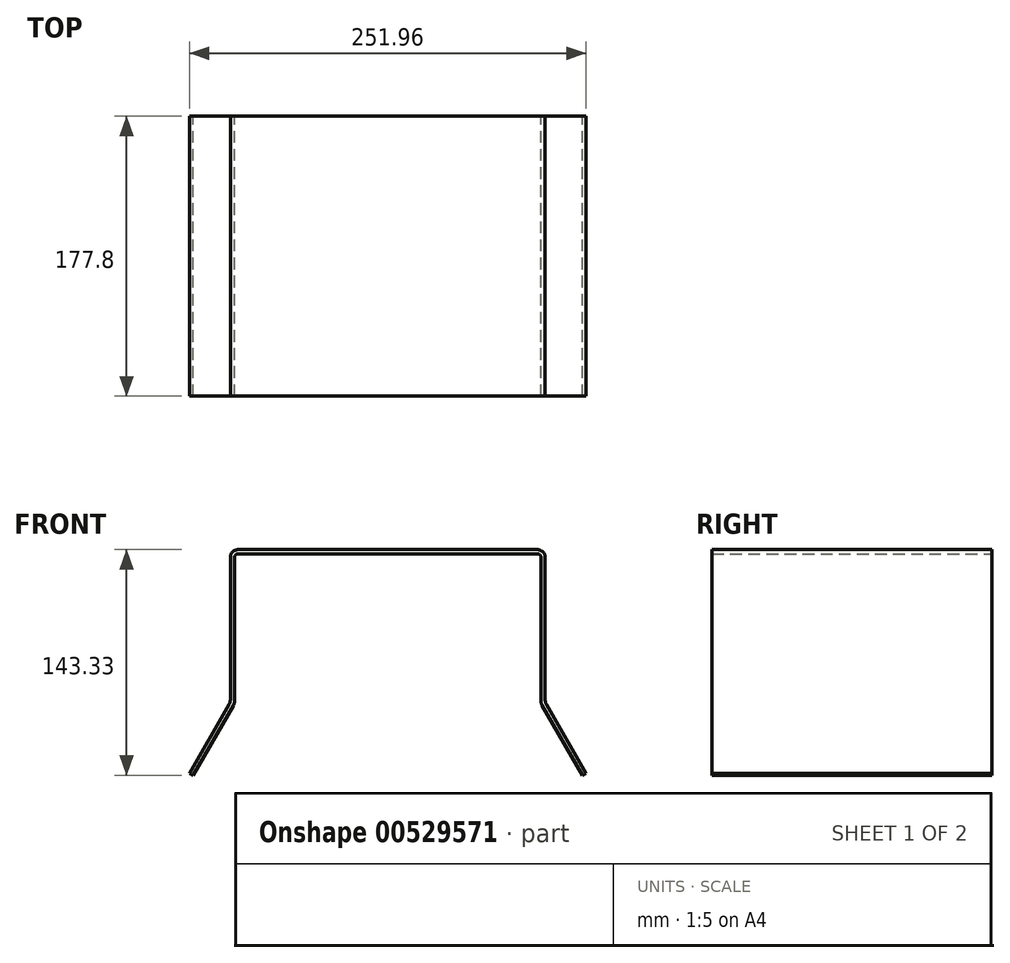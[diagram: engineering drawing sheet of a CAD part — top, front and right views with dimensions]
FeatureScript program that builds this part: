
annotation { "Feature Type Name" : "Feature", "Feature Type Description" : "" }
export const myFeature = defineFeature(function(context is Context, id is Id, definition is map)
    precondition{}
    {
        {
            var Q0;
            Q0=qCreatedBy(makeId("Front.planeOp"),FACE);
            var sketch = newSketch(context, id + "F0", { "sketchPlane" : qUnion([Q0])});
            skLineSegment(sketch, "E0", {"start": v(5, 0) * mm, "end": v(195, 0) * mm});
            skLineSegment(sketch, "E1", {"start": v(200, -5) * mm, "end": v(200, -97) * mm});
            skLineSegment(sketch, "E2", {"start": v(200, -97) * mm, "end": v(225.98, -142) * mm});
            skLineSegment(sketch, "E3", {"start": v(0, -5) * mm, "end": v(0, -97) * mm});
            skLineSegment(sketch, "E4", {"start": v(0, -97) * mm, "end": v(-25.98, -142) * mm});
            skPoint(sketch, "E5.visualSharp", {"position": v(200, 0) * mm});
            skArc(sketch, "E5.filletArc", {"start": v(200, -5) * mm, "mid": v(198.54, -1.46) * mm, "end": v(195, 0) * mm});
            skPoint(sketch, "E6.visualSharp", {"position": v(0, 0) * mm});
            skArc(sketch, "E6.filletArc", {"start": v(5, 0) * mm, "mid": v(1.46, -1.46) * mm, "end": v(0, -5) * mm});
            skLineSegment(sketch, "E7.0", {"start": v(2.65, -97.71) * mm, "end": v(-23.69, -143.33) * mm});
            skLineSegment(sketch, "E7.1", {"start": v(2.65, -5) * mm, "end": v(2.65, -97.71) * mm});
            skArc(sketch, "E7.2", {"start": v(5, -2.65) * mm, "mid": v(3.34, -3.34) * mm, "end": v(2.65, -5) * mm});
            skLineSegment(sketch, "E7.3", {"start": v(197.35, -97.71) * mm, "end": v(223.69, -143.33) * mm});
            skLineSegment(sketch, "E7.4", {"start": v(197.35, -5) * mm, "end": v(197.35, -97.71) * mm});
            skArc(sketch, "E7.5", {"start": v(197.35, -5) * mm, "mid": v(196.66, -3.34) * mm, "end": v(195, -2.65) * mm});
            skLineSegment(sketch, "E7.6", {"start": v(5, -2.65) * mm, "end": v(195, -2.65) * mm});
            skLineSegment(sketch, "E8", {"start": v(-23.69, -143.33) * mm, "end": v(-25.98, -142) * mm});
            skLineSegment(sketch, "E9", {"start": v(223.69, -143.33) * mm, "end": v(225.98, -142) * mm});
            skSolve(sketch);
        }
        {
            var Q0;
            Q0 = qSketchRegion(id + "F0", true);
            extrude(context, id + "F1", {"entities" : qUnion([Q0]), "depth" : 177.8 * mm, "offsetDistance" : 25 * mm});
        }
        {
            var Q0;
            Q0=makeQuery(id+"F1.opExtrude","SWEPT_EDGE",EDGE,{"disambiguationData":[OSD([sQuery(id+"F0.wireOp",EDGE,"E1"),sQuery(id+"F0.wireOp",EDGE,"E2")])]});
            var Q1;
            Q1=makeQuery(id+"F1.opExtrude","SWEPT_EDGE",EDGE,{"disambiguationData":[OSD([sQuery(id+"F0.wireOp",EDGE,"E7.3"),sQuery(id+"F0.wireOp",EDGE,"E7.4")])]});
            var Q2;
            Q2=makeQuery(id+"F1.opExtrude","SWEPT_EDGE",EDGE,{"disambiguationData":[OSD([sQuery(id+"F0.wireOp",EDGE,"E7.0"),sQuery(id+"F0.wireOp",EDGE,"E7.1")])]});
            var Q3;
            Q3=makeQuery(id+"F1.opExtrude","SWEPT_EDGE",EDGE,{"disambiguationData":[OSD([sQuery(id+"F0.wireOp",EDGE,"E3"),sQuery(id+"F0.wireOp",EDGE,"E4")])]});
            var Q4;
            Q4=makeQuery(id+"F1.opExtrude","SWEPT_EDGE",EDGE,{"disambiguationData":[OSD([sQuery(id+"F0.wireOp",EDGE,"E7.4"),sQuery(id+"F0.wireOp",EDGE,"E7.6")])]});
            var Q5;
            Q5=makeQuery(id+"F1.opExtrude","SWEPT_EDGE",EDGE,{"disambiguationData":[OSD([sQuery(id+"F0.wireOp",EDGE,"E7.1"),sQuery(id+"F0.wireOp",EDGE,"E7.6")])]});
            fillet(context, id + "F2", {"entities" : qUnion([Q0, Q1, Q2, Q3, Q4, Q5]), "radius" : 5 * mm, "tangentPropagation" : true, "allowEdgeOverflow" : false});
        }
    });
